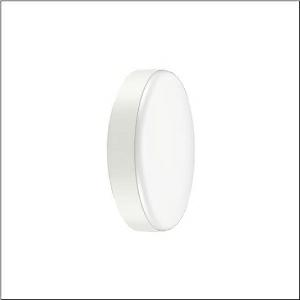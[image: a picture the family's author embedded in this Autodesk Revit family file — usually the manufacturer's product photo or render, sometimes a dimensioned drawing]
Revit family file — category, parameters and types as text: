
# Revit family: rondel_31_51wc10mb44as
name_source: partatom
category: Lighting Fixtures
units: mm (PartAtom-declared; Revit-internal decimal feet)

## family parameters
Cut with Voids When Loaded = No
Host = Face
Light Source = No
Part Type = Normal
Room Calculation Point = No
Round Connector Dimension = Use Diameter
Shared = No

## types (1)
- --- (1 x LED, 4400 lm, 35.5 W, 4000K)
    Apparent Load = 36 VA
    CIE Flux Codes = 44 75 94 94 100
    Color Rendering = 80
    Color Temperature = 4000K
    Default Elevation = 1800 mm
    Description = Rondel 31, wall and ceiling luminaire, primary optical cover: cover, of PC, opal, light emission: direct distribution, primary light characteristic: symmetric, installation type: surface-mounted, LED, rated luminous flux: 4.250lm, luminous efficacy: 117lm/W, light colour: 840, colour temperature: 4000K, with terminal, 3-pole, max. 2.5mm², mains connection: 220..240V, AC, 50/60Hz, rated input power: 35.5W, luminaire housing, of PC, traffic white (RAL 9016), diameter: 480mm, brightness and presence sensor, HF sensor, protection rating (complete): IP65, insulation class (complete): insulation class II (safety insulation), certification: CE, impact resistance: IK10, permissible storage temperature: -20..+60°C, packaging unit: 1 piece
    Height = 97 mm
    Lamp = 1 x LED
    Lamp Light Flux = 4400 lm
    Lamp Power = 35.5 W
    Lamp count = 1
    Length = 480 mm
    Luminous efficacy = 124 lm/W
    Manufacturer = Siteco
    ModVariant = No
    Model = 51WC10MB44AS
    Mounting Place = Ceiling
    Mounting Type = Surface mounted
    Number of Poles = 1
    OnlyDefault = Yes
    Power Factor = 1
    Product Name = Rondel 31
    Product group = wall and ceiling luminaire
    ProductGroupID = 301
    Protection Class = Protection class II
    Protection Degree = IP 65
    RLX_Detail_Level = 1
    RlxData = <blob elided: 41369 chars, md5=0697315b>
    Socket = socket
    Standby Power = 0 W
    System Light Flux = 4400 lm
    System Power = 36 W
    Type Comments = factory setting: luminous flux: 100 % | (ON | ON)
    Type Image = l_1007188.jpg
    URL = http://relux.com
    VarID = @adj_060545
    Voltage = 0 V
    Weight = 0.00 kg
    Width = 0 mm  [stored 0 ft]

note: [stored X ft] marks values corroborated as IEEE doubles in the binary element streams (Revit-internal decimal feet)

## geometry (parser evidence)
native form markers: Blend x4, Sweep x13
no freeform markers — native parametric forms only
